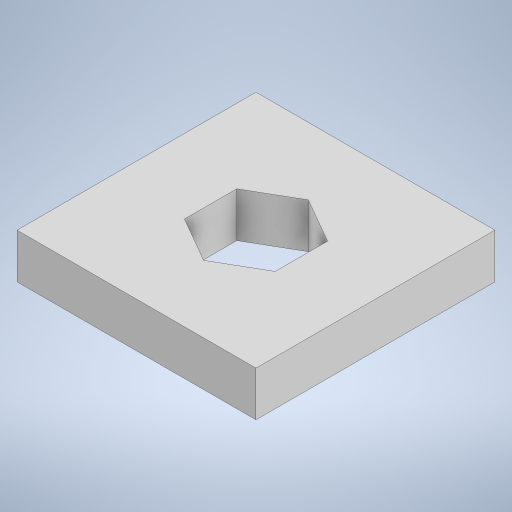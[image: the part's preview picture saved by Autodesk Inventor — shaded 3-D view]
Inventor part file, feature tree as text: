
AUTODESK INVENTOR PART (.ipt)
format: ipt  version: 2023 (Build 270158000, 158)  size: 206,336 bytes
history: native  units: in
note: dims shown in document units (in); Inventor stores cm internally (conversion verified against a paired STEP export)
features: extrude x1, sketch x1
ambient origin geometry x8: Origin, YZ Plane, XZ Plane, XY Plane, X Axis, Y Axis, Z Axis, Center Point
bodies: Solid1 (feature_tree)
feature tree (2):
  extrude  "Extrusion1"  Depth=2.0in
  sketch  "Sketch1"  dims[d0=2.0in d1=2.0in d2=0.6575in d3=0.375in d4=0.0in]
